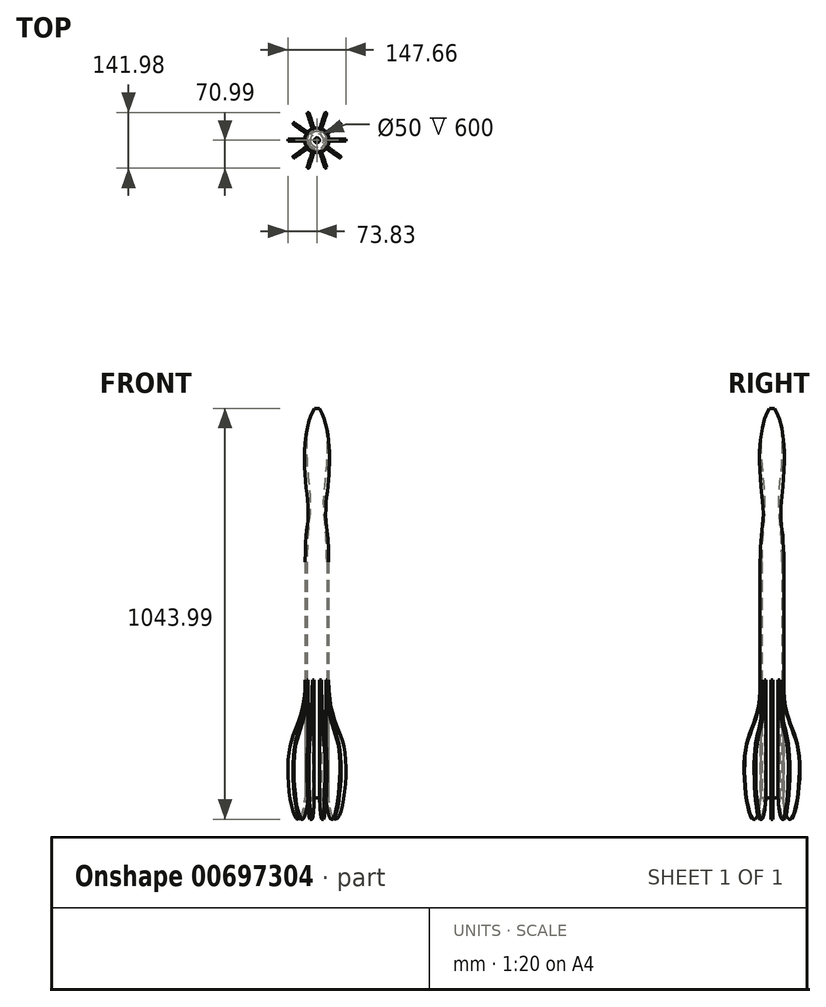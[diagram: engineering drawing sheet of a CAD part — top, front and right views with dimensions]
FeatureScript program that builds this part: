
annotation { "Feature Type Name" : "Feature", "Feature Type Description" : "" }
export const myFeature = defineFeature(function(context is Context, id is Id, definition is map)
    precondition{}
    {
        {
            var Q0;
            Q0=qCreatedBy(makeId("Front.planeOp"),FACE);
            var sketch = newSketch(context, id + "F0", { "sketchPlane" : qUnion([Q0])});
            skLineSegment(sketch, "E0", {"start": v(-25, -271.11) * mm, "end": v(-25, 328.89) * mm});
            skLineSegment(sketch, "E1", {"start": v(-30, 328.89) * mm, "end": v(-30, -271.11) * mm});
            skLineSegment(sketch, "E2", {"start": v(0, -271.11) * mm, "end": v(0, 727.57) * mm, "construction": true});
            skFitSpline(sketch, "E3", {"points": [v(0, 727.57) * mm, v(-26.29, 598.23) * mm, v(-17.23, 478.63) * mm, v(-25, 328.89) * mm], "startDerivative": vector(-226.86, -272.42) * mm, "endDerivative": vector(0, -671.14) * mm});
            skFitSpline(sketch, "E4", {"points": [v(0, 727.57) * mm, v(-31.26, 572.91) * mm, v(-22.23, 453.61) * mm, v(-30, 328.89) * mm], "startDerivative": vector(-226.86, -272.42) * mm, "endDerivative": vector(0, -671.26) * mm});
            skFitSpline(sketch, "E5", {"points": [v(-30, 28.89) * mm, v(-70.65, -150.49) * mm, v(-52.88, -322.5) * mm, v(-30, -271.11) * mm], "startDerivative": vector(0, -786.2) * mm, "endDerivative": vector(59.74, 605.78) * mm});
            skLineSegment(sketch, "E6", {"start": v(-25, -271.11) * mm, "end": v(-30, -271.11) * mm});
            skFitSpline(sketch, "E7", {"points": [v(-25.86, 647.34) * mm, v(0, 720.45) * mm, v(25.86, 647.34) * mm], "startDerivative": vector(51.72, 219.34) * mm, "endDerivative": vector(51.72, -219.34) * mm});
            skPoint(sketch, "E8.MirrorCS.end.orphan", {"position": v(25, 328.89) * mm});
            skPoint(sketch, "E9.MirrorCS.start.orphan", {"position": v(30, 328.89) * mm});
            skLineSegment(sketch, "E10", {"start": v(0, 720.45) * mm, "end": v(0, 727.57) * mm});
            skLineSegment(sketch, "E11", {"start": v(-11, -325.12) * mm, "end": v(-85.43, -325.12) * mm, "construction": true});
            skLineSegment(sketch, "E12", {"start": v(76.48, 647.37) * mm, "end": v(-104.97, 647.64) * mm, "construction": true});
            skSolve(sketch);
        }
        {
            var Q0;
            Q0=makeQuery(id+"F0.imprint","IMPRINT",FACE,{"disambiguationData":[TD([[makeQuery(id+"F0.imprint","IMPRINT",EDGE,{"derivedFrom":sQuery(id+"F0.wireOp",EDGE,"E0")}),1.0]])]});
            var Q1;
            Q1=sQuery(id+"F0.wireOp",EDGE,"E2");
            revolve(context, id + "F1", {"entities" : qUnion([Q0]), "axis" : qUnion([Q1]), "revolveType" : RevolveType.FULL});
        }
        {
            var Q0;
            {var subQ0=sQuery(id+"F0.wireOp",EDGE,"E5");Q0=makeQuery(id+"F0.imprint","IMPRINT",FACE,{"disambiguationData":[TD([[makeQuery(id+"F0.imprint","IMPRINT",EDGE,{"derivedFrom":subQ0}),1.0]])]});}
            extrude(context, id + "F2", {"entities" : qUnion([Q0]), "operationType" : NewBodyOperationType.ADD, "endBound" : BoundingType.SYMMETRIC, "depth" : 5 * mm, "offsetDistance" : 25 * mm});
        }
        {
            var Q0;
            Q0=makeQuery(id+"F2.opExtrude","SWEPT_BODY",BODY,{"disambiguationData":[OSD([sQuery(id+"F0.wireOp",EDGE,"E1"),sQuery(id+"F0.wireOp",EDGE,"E5")])]});
            var Q1;
            Q1=makeQuery(id+"F1.opRevolve","SWEPT_FACE",FACE,{"disambiguationData":[OSD([sQuery(id+"F0.wireOp",EDGE,"E1")])]});
            circularPattern(context, id + "F3", {"entities" : qUnion([Q0]), "axis" : qUnion([Q1]), "angle" : 360 * degree, "instanceCount" : 10, "equalSpace" : true, "isCentered" : true});
        }
    });
